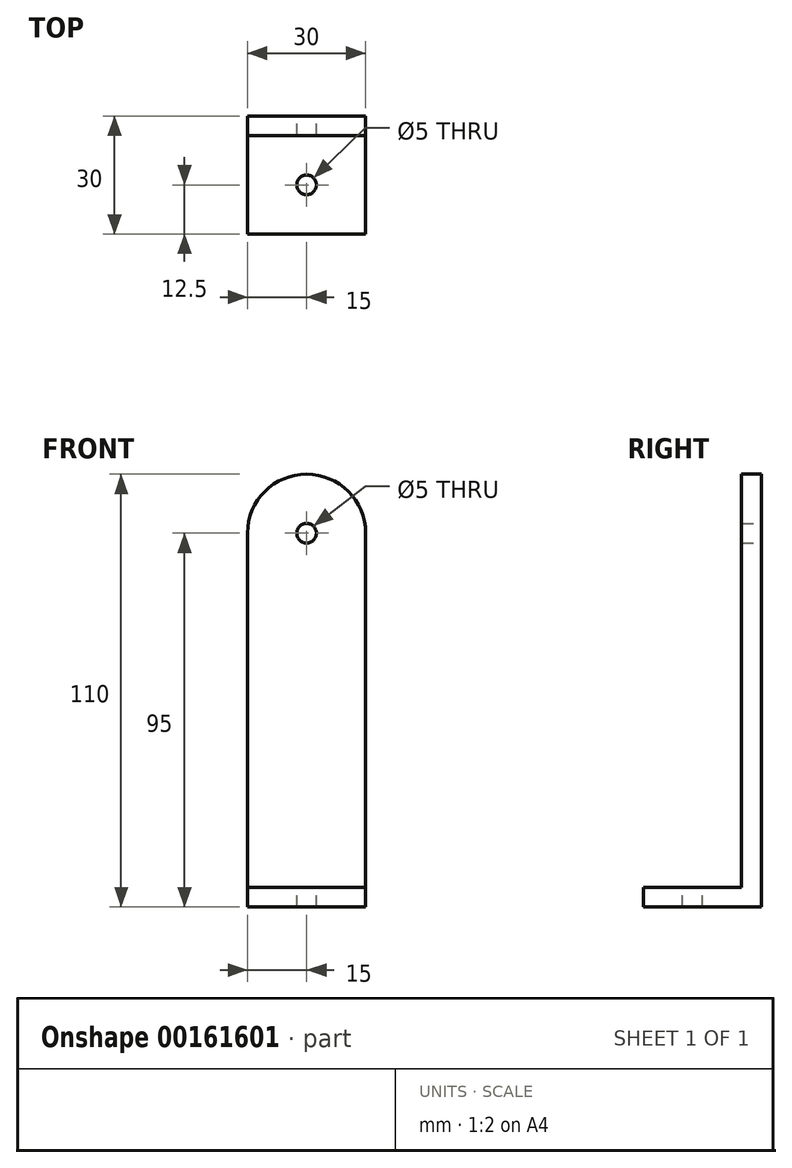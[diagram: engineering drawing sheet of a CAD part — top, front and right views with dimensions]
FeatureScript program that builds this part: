
annotation { "Feature Type Name" : "Feature", "Feature Type Description" : "" }
export const myFeature = defineFeature(function(context is Context, id is Id, definition is map)
    precondition{}
    {
        {
            var Q0;
            Q0=qCreatedBy(makeId("Front.planeOp"),FACE);
            var sketch = newSketch(context, id + "F0", { "sketchPlane" : qUnion([Q0])});
            skLineSegment(sketch, "E0.bottom", {"start": v(-15, 47.5) * mm, "end": v(15, 47.5) * mm, "construction": true});
            skLineSegment(sketch, "E0.top", {"start": v(-15, -47.5) * mm, "end": v(15, -47.5) * mm});
            skLineSegment(sketch, "E0.left", {"start": v(-15, 47.5) * mm, "end": v(-15, -47.5) * mm});
            skLineSegment(sketch, "E0.right", {"start": v(15, 47.5) * mm, "end": v(15, -47.5) * mm});
            skPoint(sketch, "E0.middle", {"position": v(0, 0) * mm});
            skArc(sketch, "E1", {"start": v(-15, 47.5) * mm, "mid": v(0, 62.5) * mm, "end": v(15, 47.5) * mm});
            skCircle(sketch, "E2", {"center": v(0, 47.5) * mm, "radius": 2.5 * mm});
            skSolve(sketch);
        }
        {
            var Q0;
            Q0 = qSketchRegion(id + "F0", true);
            extrude(context, id + "F1", {"entities" : qUnion([Q0]), "endBound" : BoundingType.SYMMETRIC, "depth" : 5 * mm});
        }
        {
            var Q0;
            Q0=makeQuery(id+"F1.opExtrude","CAP_FACE",FACE,{"disambiguationData":[OSD([sQuery(id+"F0.wireOp",EDGE,"E0.top"),sQuery(id+"F0.wireOp",EDGE,"E0.left"),sQuery(id+"F0.wireOp",EDGE,"E0.right"),sQuery(id+"F0.wireOp",EDGE,"E1"),sQuery(id+"F0.wireOp",EDGE,"E2")])],"isStart":false});
            var sketch = newSketch(context, id + "F2", { "sketchPlane" : qUnion([Q0])});
            skLineSegment(sketch, "E3.bottom", {"start": v(-15, -47.5) * mm, "end": v(15, -47.5) * mm});
            skLineSegment(sketch, "E3.top", {"start": v(-15, -42.5) * mm, "end": v(15, -42.5) * mm});
            skLineSegment(sketch, "E3.left", {"start": v(-15, -47.5) * mm, "end": v(-15, -42.5) * mm});
            skLineSegment(sketch, "E3.right", {"start": v(15, -47.5) * mm, "end": v(15, -42.5) * mm});
            skSolve(sketch);
        }
        {
            var Q0;
            Q0 = qSketchRegion(id + "F2", true);
            extrude(context, id + "F3", {"entities" : qUnion([Q0]), "operationType" : NewBodyOperationType.ADD, "depth" : 25 * mm});
        }
        {
            var Q0;
            Q0=makeQuery(id+"F3.opExtrude","SWEPT_FACE",FACE,{"disambiguationData":[OSD([sQuery(id+"F2.wireOp",EDGE,"E3.top")])]});
            var sketch = newSketch(context, id + "F4", { "sketchPlane" : qUnion([Q0])});
            skPoint(sketch, "E4", {"position": v(-15, -15) * mm});
            skCircle(sketch, "E5", {"center": v(0, -15) * mm, "radius": 2.5 * mm});
            skSolve(sketch);
        }
        {
            var Q0;
            Q0 = qSketchRegion(id + "F4", true);
            extrude(context, id + "F5", {"entities" : qUnion([Q0]), "operationType" : NewBodyOperationType.REMOVE, "endBound" : BoundingType.UP_TO_NEXT, "oppositeDirection" : true, "depth" : 25 * mm});
        }
    });
